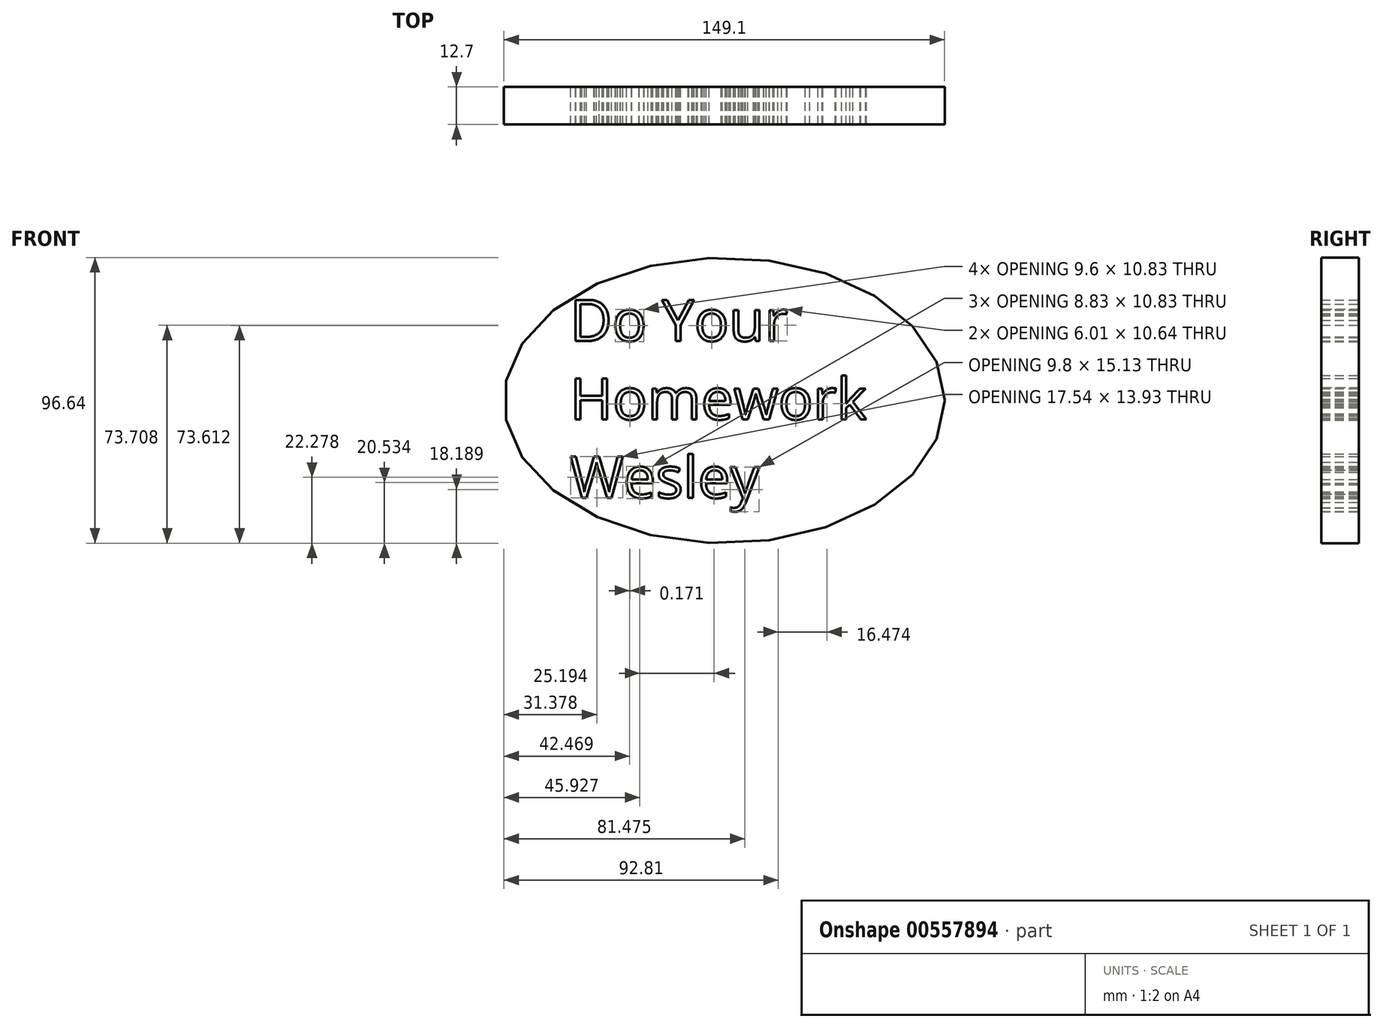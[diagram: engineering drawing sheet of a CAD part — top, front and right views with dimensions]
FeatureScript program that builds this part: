
annotation { "Feature Type Name" : "Feature", "Feature Type Description" : "" }
export const myFeature = defineFeature(function(context is Context, id is Id, definition is map)
    precondition{}
    {
        {
            var Q0;
            Q0=qCreatedBy(makeId("Front.planeOp"),FACE);
            var sketch = newSketch(context, id + "F0", { "sketchPlane" : qUnion([Q0])});
            skEllipse(sketch, "E0", {"center": v(1.44, 0) * mm, "majorRadius": 74.55 * mm, "minorRadius": 48.32 * mm, "majorAxis": v(1, 0)});
            skSolve(sketch);
        }
        {
            var Q0;
            Q0 = qSketchRegion(id + "F0", true);
            var Q1;
            Q1=makeQuery(id+"F0.imprint","IMPRINT",FACE,{"disambiguationData":[TD([[makeQuery(id+"F0.imprint","IMPRINT",EDGE,{"derivedFrom":sQuery(id+"F0.wireOp",EDGE,"E0")}),1.0]])]});
            extrude(context, id + "F1", {"entities" : qUnion([Q0, Q1]), "depth" : 12.7 * mm, "offsetDistance" : 25.4 * mm});
        }
        {
            var Q0;
            Q0=qCreatedBy(makeId("Front.planeOp"),FACE);
            var sketch = newSketch(context, id + "F2", { "sketchPlane" : qUnion([Q0])});
            skText(sketch, "E1", { "text": "Do Your\nHomework\nWesley", "fontName": "OpenSans-Regular.ttf"});
            const initialGuessF2  = {"E1": [-0.05076, 0.02007, 1, 0, 0.01405]};
            skSetInitialGuess(sketch, initialGuessF2);
            skSolve(sketch);
        }
        {
            var Q0;
            Q0 = qSketchRegion(id + "F2", true);
            extrude(context, id + "F3", {"entities" : qUnion([Q0]), "operationType" : NewBodyOperationType.REMOVE, "depth" : 25.4 * mm, "offsetDistance" : 25.4 * mm});
        }
    });
